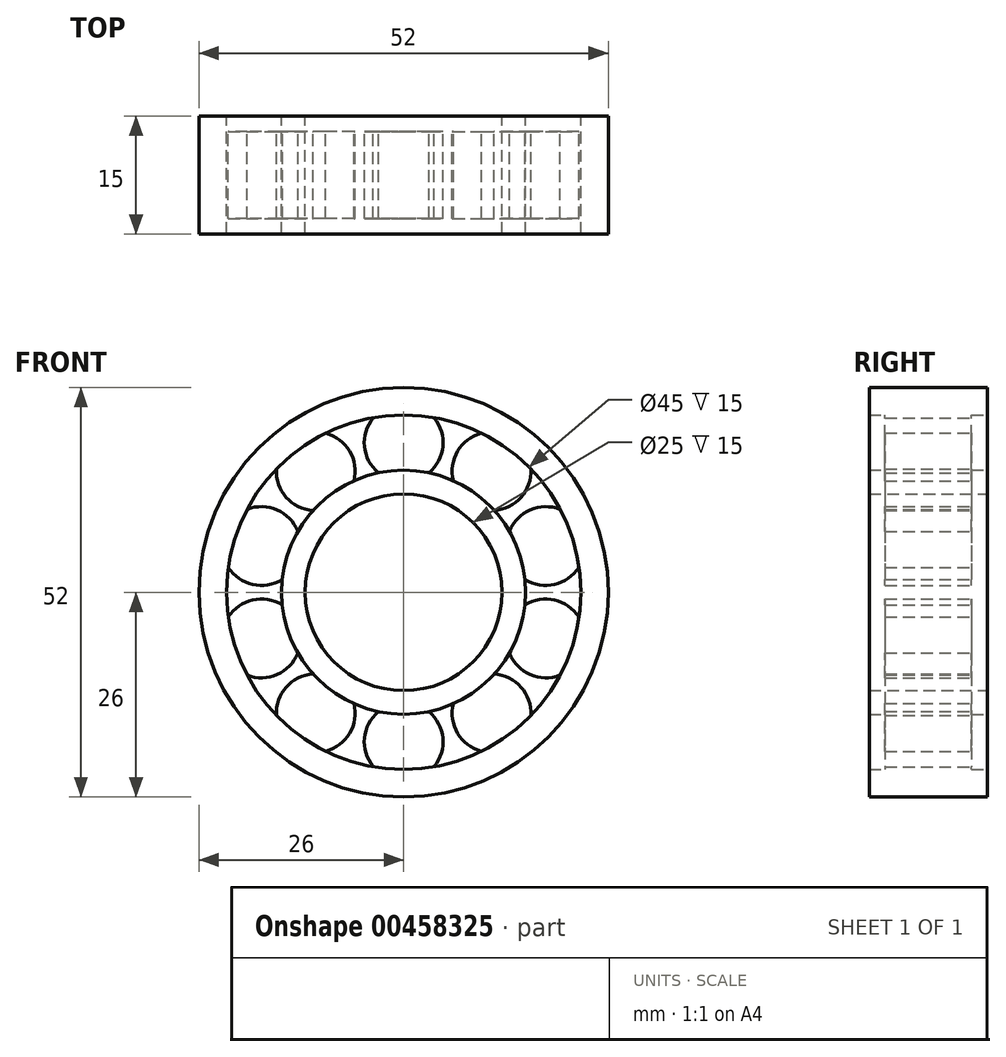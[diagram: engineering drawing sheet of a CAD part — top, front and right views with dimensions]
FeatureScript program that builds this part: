
annotation { "Feature Type Name" : "Feature", "Feature Type Description" : "" }
export const myFeature = defineFeature(function(context is Context, id is Id, definition is map)
    precondition{}
    {
        {
            var Q0;
            Q0=qCreatedBy(makeId("Front.planeOp"),FACE);
            var sketch = newSketch(context, id + "F0", { "sketchPlane" : qUnion([Q0])});
            skCircle(sketch, "E0", {"center": v(0, 0) * mm, "radius": 22.5 * mm});
            skCircle(sketch, "E1", {"center": v(0, 0) * mm, "radius": 26 * mm});
            skSolve(sketch);
        }
        {
            var Q0;
            Q0 = qSketchRegion(id + "F0", true);
            extrude(context, id + "F1", {"entities" : qUnion([Q0]), "depth" : 15 * mm});
        }
        {
            var Q0;
            Q0=qCreatedBy(makeId("Front.planeOp"),FACE);
            var sketch = newSketch(context, id + "F2", { "sketchPlane" : qUnion([Q0])});
            skCircle(sketch, "E2", {"center": v(0, 0) * mm, "radius": 12.5 * mm});
            skCircle(sketch, "E3", {"center": v(0, 0) * mm, "radius": 15.5 * mm});
            skSolve(sketch);
        }
        {
            var Q0;
            Q0 = qSketchRegion(id + "F2", true);
            extrude(context, id + "F3", {"entities" : qUnion([Q0]), "depth" : 15 * mm});
        }
        {
            var Q0;
            Q0=qCreatedBy(makeId("Front.planeOp"),FACE);
            cPlane(context, id + "F4", {"entities" : qUnion([Q0]), "cplaneType" : CPlaneType.OFFSET, "offset" : 7.5 * mm, "width" : 150 * mm, "height" : 150 * mm});
        }
        {
            var Q0;
            Q0=qCreatedBy(id+"F4.planeOp",FACE);
            var sketch = newSketch(context, id + "F5", { "sketchPlane" : qUnion([Q0])});
            skCircle(sketch, "E4", {"center": v(0, 19) * mm, "radius": 5 * mm});
            skCircle(sketch, "E5.1.0", {"center": v(-11.17, 15.37) * mm, "radius": 5 * mm});
            skCircle(sketch, "E5.2.0", {"center": v(-18.07, 5.87) * mm, "radius": 5 * mm});
            skCircle(sketch, "E5.3.0", {"center": v(-18.07, -5.87) * mm, "radius": 5 * mm});
            skCircle(sketch, "E5.4.0", {"center": v(-11.17, -15.37) * mm, "radius": 5 * mm});
            skCircle(sketch, "E5.5.0", {"center": v(0, -19) * mm, "radius": 5 * mm});
            skCircle(sketch, "E5.6.0", {"center": v(11.17, -15.37) * mm, "radius": 5 * mm});
            skCircle(sketch, "E5.7.0", {"center": v(18.07, -5.87) * mm, "radius": 5 * mm});
            skCircle(sketch, "E5.8.0", {"center": v(18.07, 5.87) * mm, "radius": 5 * mm});
            skCircle(sketch, "E5.9.0", {"center": v(11.17, 15.37) * mm, "radius": 5 * mm});
            skPoint(sketch, "E5.center", {"position": v(0, 0) * mm});
            skSolve(sketch);
        }
        {
            var Q0;
            Q0=makeQuery(id+"F5.imprint","IMPRINT",FACE,{"disambiguationData":[TD([[makeQuery(id+"F5.imprint","IMPRINT",EDGE,{"derivedFrom":sQuery(id+"F5.wireOp",EDGE,"E5.1.0")}),1.0]])]});
            var Q1;
            Q1=makeQuery(id+"F5.imprint","IMPRINT",FACE,{"disambiguationData":[TD([[makeQuery(id+"F5.imprint","IMPRINT",EDGE,{"derivedFrom":sQuery(id+"F5.wireOp",EDGE,"E4")}),1.0]])]});
            var Q2;
            Q2=makeQuery(id+"F5.imprint","IMPRINT",FACE,{"disambiguationData":[TD([[makeQuery(id+"F5.imprint","IMPRINT",EDGE,{"derivedFrom":sQuery(id+"F5.wireOp",EDGE,"E5.2.0")}),1.0]])]});
            var Q3;
            Q3=makeQuery(id+"F5.imprint","IMPRINT",FACE,{"disambiguationData":[TD([[makeQuery(id+"F5.imprint","IMPRINT",EDGE,{"derivedFrom":sQuery(id+"F5.wireOp",EDGE,"E5.3.0")}),1.0]])]});
            var Q4;
            Q4=makeQuery(id+"F5.imprint","IMPRINT",FACE,{"disambiguationData":[TD([[makeQuery(id+"F5.imprint","IMPRINT",EDGE,{"derivedFrom":sQuery(id+"F5.wireOp",EDGE,"E5.4.0")}),1.0]])]});
            var Q5;
            Q5=makeQuery(id+"F5.imprint","IMPRINT",FACE,{"disambiguationData":[TD([[makeQuery(id+"F5.imprint","IMPRINT",EDGE,{"derivedFrom":sQuery(id+"F5.wireOp",EDGE,"E5.5.0")}),1.0]])]});
            var Q6;
            Q6=makeQuery(id+"F5.imprint","IMPRINT",FACE,{"disambiguationData":[TD([[makeQuery(id+"F5.imprint","IMPRINT",EDGE,{"derivedFrom":sQuery(id+"F5.wireOp",EDGE,"E5.6.0")}),1.0]])]});
            var Q7;
            Q7=makeQuery(id+"F5.imprint","IMPRINT",FACE,{"disambiguationData":[TD([[makeQuery(id+"F5.imprint","IMPRINT",EDGE,{"derivedFrom":sQuery(id+"F5.wireOp",EDGE,"E5.7.0")}),1.0]])]});
            var Q8;
            Q8=makeQuery(id+"F5.imprint","IMPRINT",FACE,{"disambiguationData":[TD([[makeQuery(id+"F5.imprint","IMPRINT",EDGE,{"derivedFrom":sQuery(id+"F5.wireOp",EDGE,"E5.8.0")}),1.0]])]});
            var Q9;
            Q9=makeQuery(id+"F5.imprint","IMPRINT",FACE,{"disambiguationData":[TD([[makeQuery(id+"F5.imprint","IMPRINT",EDGE,{"derivedFrom":sQuery(id+"F5.wireOp",EDGE,"E5.9.0")}),1.0]])]});
            extrude(context, id + "F6", {"entities" : qUnion([Q0, Q1, Q2, Q3, Q4, Q5, Q6, Q7, Q8, Q9]), "operationType" : NewBodyOperationType.ADD, "depth" : 11 * mm, "symmetric" : true});
        }
    });
